# Revit family: FR_PG-EVO_Fondation_V1-2
name_source: partatom
category: Allgemeines Modell
revit_build: Autodesk Revit 2018 (Build: 20181015_0930(x64)
units: mm (PartAtom-declared; Revit-internal decimal feet)

## family parameters
Beim Laden mit Abzugskörper schneiden = Ja
Bemaßung runder Anschluss = Durchmesser verwenden
Gemeinsam genutzt = Ja
Kann Basisbauteil für Bewehrung sein = Nein
Raumberechnungspunkt = Nein
Teiletyp = Normal

## types (1)
- MEARIN PG EVO-V1_2 Mörtelbett
    Bauelement = Élément de drainage surface de l'eau
    Beschreibung = Système de drainage en composite armé de fibres de verre, largeur totale 170 (AS) ou 180 (OS) mm.
Hauteur 30 mm - Réduction des raccords de jonctions grâce à une longueur de 3000 mm.
Disponible en 3 couleurs standard (gris, noir et rouge)**. Autres couleurs sur demande (à partir de 1000m)
Classes de charge A 15 à C250 selon norme EN 1433. Respectez les conseils de pose MEA.
    Construction Élement de drainage = Caniveau profile peigne
    Documents de mise en œuvre = conformément aux dessins et à la description du produits
    Fiche technique produit = https://www.mea-group.com
    Hersteller = MEA Bautechnik GmbH business unite MEA Water Management
    IfcDescription = Système de drainage en composite armé de fibres de verre, largeur totale 170 (AS) ou 180 (OS) mm.
Hauteur 30 mm - Réduction des raccords de jonctions grâce à une longueur de 3000 mm.
Disponible en 3 couleurs standard (gris, noir et rouge)**. Autres couleurs sur demande (à partir de 1000m)
Classes de charge A 15 à C250 selon norme EN 1433. Respectez les conseils de pose MEA.
    IfcExportAs = IfcWasteTerminalType
    IfcExportType = USERDEFINED
    Largeur = 180 mm  [stored 0.590551 ft]
    Largeur utile = 150 mm  [stored 0.492126 ft]
    Largeur utile de l'élément de drainage mm = 150
    MEA aide montage = https://www.mea-group.com
    Materiaux, dénrobage/ de fondation = PCC-Mörtel/Epoxy-Mörtel
    Poids = voir la densité du mortier
    Référence (Art.Nr) = 010141803
    STLB-exemplaire = https://www.stlb-bau-online.de
    Technique de montage = Caniveau seul
    Type Élement de drainage = Typ M
    URL = https://www.mea-group.com
    classe de charge del'élément de drainage = C 250
    guid = cf6c1bd8-9bf4-4563-8c57-07955e2378ac
    max. Hauteur du sol = 60mm
    min. Hauteur de sol = 40mm
    élément de construction, de drainage = Caniveau de drainage

note: [stored X ft] marks values corroborated as IEEE doubles in the binary element streams (Revit-internal decimal feet)
